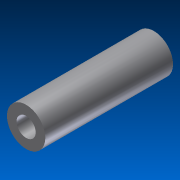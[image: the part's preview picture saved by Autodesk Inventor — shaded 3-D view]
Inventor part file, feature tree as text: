
AUTODESK INVENTOR PART (.ipt)
format: ipt  version: 2012 (Build 160160000, 160)  size: 79,360 bytes
history: native  units: in
note: dims shown in document units (in); Inventor stores cm internally (conversion verified against a paired STEP export)
features: extrude x1, sketch x1
ambient origin geometry x8: Origin, YZ Plane, XZ Plane, XY Plane, X Axis, Y Axis, Z Axis, Center Point
bodies: Solid1 (feature_tree)
feature tree (2):
  extrude  "Extrusion1"  Depth=0.2362in
  sketch  "Sketch1"  dims[d0=0.1181in d1=0.2362in d2=0.7874in d3=0.0in]
